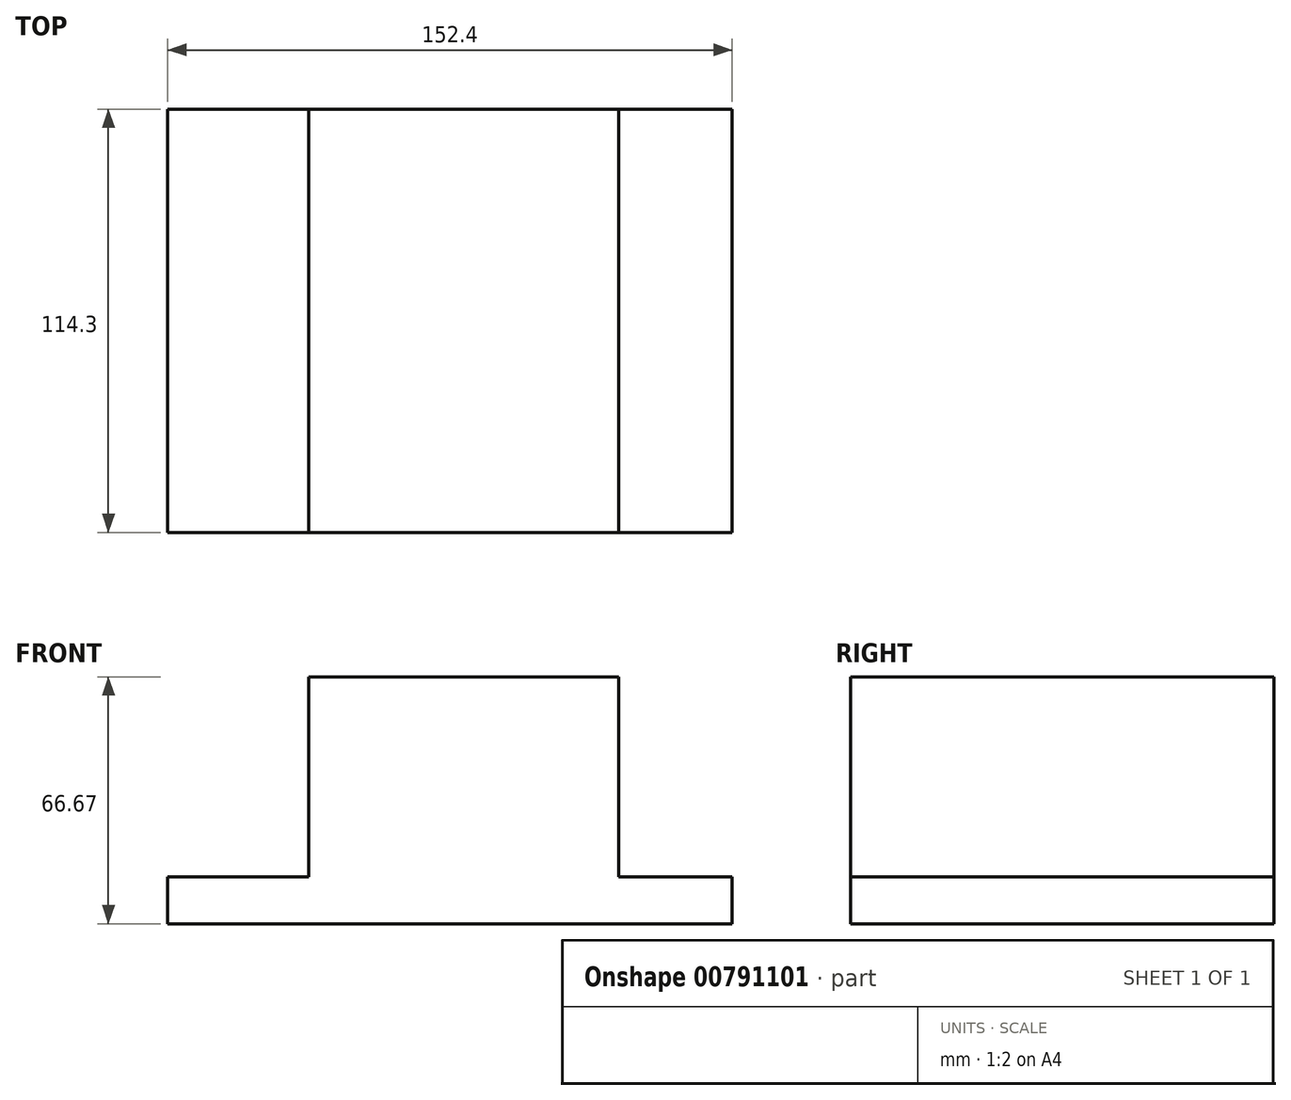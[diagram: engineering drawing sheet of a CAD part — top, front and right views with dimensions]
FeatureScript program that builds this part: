
annotation { "Feature Type Name" : "Feature", "Feature Type Description" : "" }
export const myFeature = defineFeature(function(context is Context, id is Id, definition is map)
    precondition{}
    {
        {
            var Q0;
            Q0=qCreatedBy(makeId("Front.planeOp"),FACE);
            var sketch = newSketch(context, id + "F0", { "sketchPlane" : qUnion([Q0])});
            skLineSegment(sketch, "E0", {"start": v(0.39, 0) * mm, "end": v(152.79, 0) * mm});
            skLineSegment(sketch, "E1", {"start": v(0.39, 0) * mm, "end": v(0.39, 12.7) * mm});
            skLineSegment(sketch, "E2", {"start": v(152.79, 0) * mm, "end": v(152.79, 12.7) * mm});
            skLineSegment(sketch, "E3", {"start": v(0.39, 12.7) * mm, "end": v(38.49, 12.7) * mm});
            skLineSegment(sketch, "E4", {"start": v(152.79, 12.7) * mm, "end": v(122.17, 12.7) * mm});
            skLineSegment(sketch, "E5", {"start": v(38.49, 12.7) * mm, "end": v(38.49, 66.68) * mm});
            skLineSegment(sketch, "E6", {"start": v(122.17, 12.7) * mm, "end": v(122.17, 66.68) * mm});
            skLineSegment(sketch, "E7", {"start": v(38.49, 66.68) * mm, "end": v(122.17, 66.68) * mm});
            skSolve(sketch);
        }
        {
            var Q0;
            Q0=makeQuery(id+"F0.imprint","IMPRINT",FACE,{"disambiguationData":[TD([[makeQuery(id+"F0.imprint","IMPRINT",EDGE,{"derivedFrom":sQuery(id+"F0.wireOp",EDGE,"E0")}),1.0]])]});
            extrude(context, id + "F1", {"entities" : qUnion([Q0]), "depth" : 114.3 * mm, "offsetDistance" : 25.4 * mm});
        }
    });
